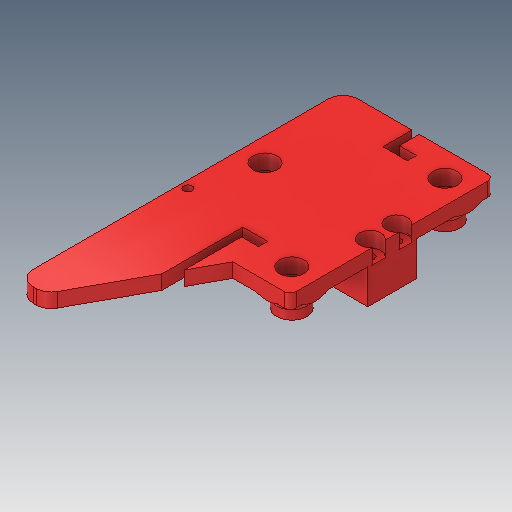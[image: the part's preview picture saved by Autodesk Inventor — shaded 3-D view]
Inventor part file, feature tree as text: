
AUTODESK INVENTOR PART (.ipt)
format: ipt  version: 2019.4 (Build 234330000, 330)  size: 252,416 bytes
history: native  units: mm
features: sketch x7, other x3, plane x2
ambient origin geometry x8: Origin, YZ Plane, XZ Plane, XY Plane, X Axis, Y Axis, Z Axis, Center Point
bodies: Solid1 (feature_tree)
feature tree (12):
  other  "Neje_Base_Slide_y_20mmrod.ipt"
  other  "Solid1::Neje_Base_Slide_y_20mmrod.ipt"
  other  "TaggingFeature1"
  sketch  "Sketch1"  dims[d0=10.0mm]
  sketch  "Sketch2"
  sketch  "Sketch4"
  sketch  "Sketch5"
  sketch  "Sketch6"
  sketch  "Sketch11"
  sketch  "Sketch13"
  plane  "Work Plane2"
  plane  "Work Plane3"
